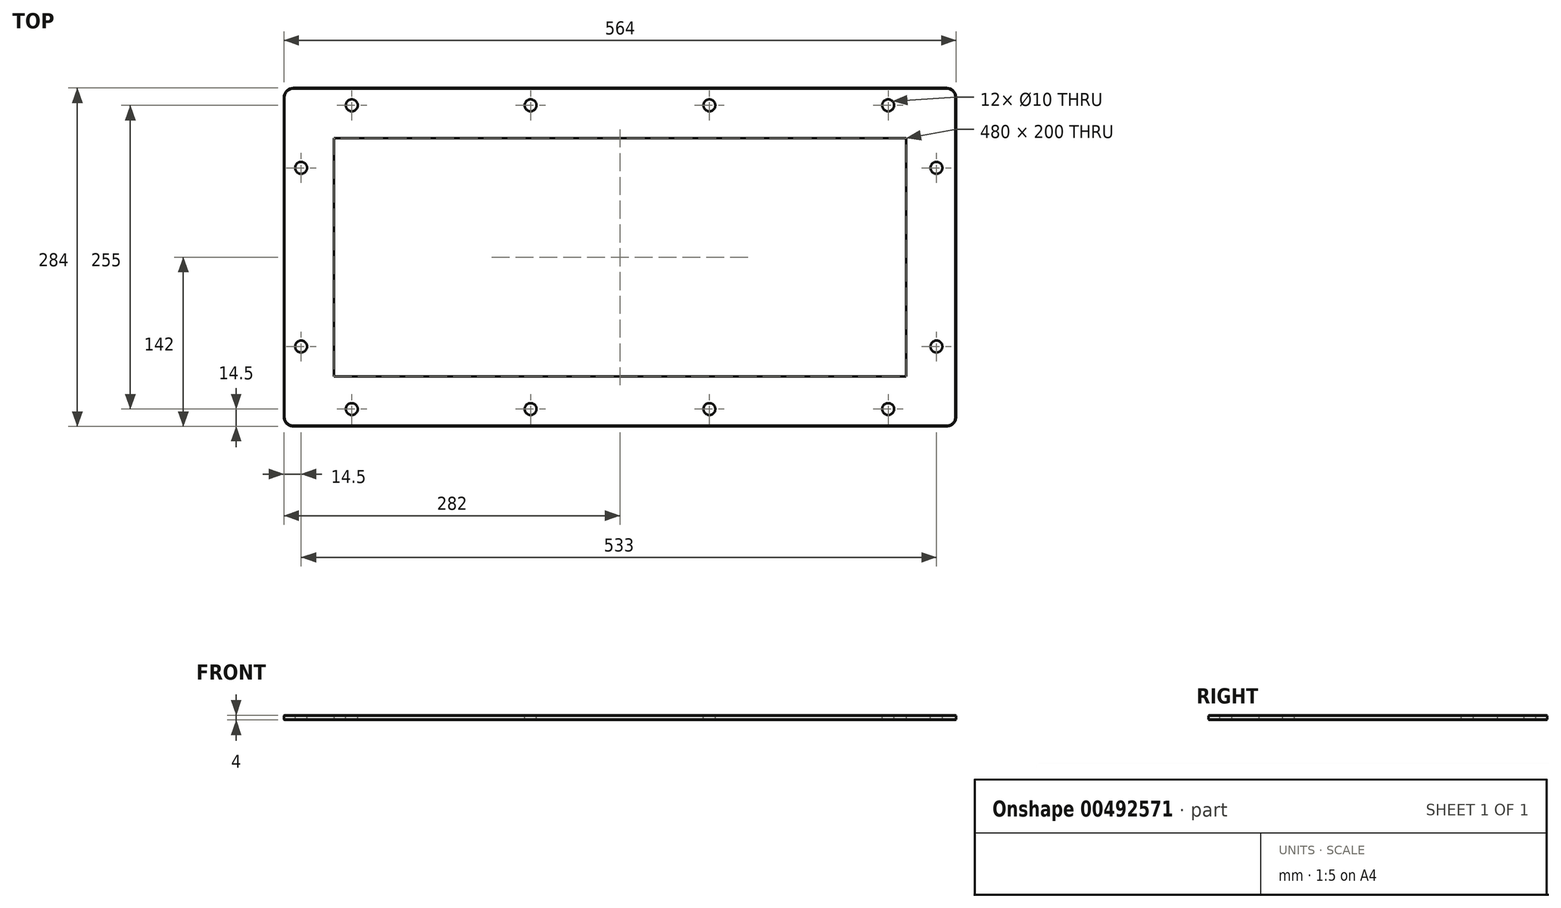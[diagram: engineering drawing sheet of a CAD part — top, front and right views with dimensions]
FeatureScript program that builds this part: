
annotation { "Feature Type Name" : "Feature", "Feature Type Description" : "" }
export const myFeature = defineFeature(function(context is Context, id is Id, definition is map)
    precondition{}
    {
        {
            var Q0;
            Q0=qCreatedBy(makeId("Top.planeOp"),FACE);
            var sketch = newSketch(context, id + "F0", { "sketchPlane" : qUnion([Q0])});
            skLineSegment(sketch, "E0.bottom", {"start": v(274, -142) * mm, "end": v(-274, -142) * mm});
            skLineSegment(sketch, "E0.top", {"start": v(274, 142) * mm, "end": v(-274, 142) * mm});
            skLineSegment(sketch, "E0.left", {"start": v(282, -134) * mm, "end": v(282, 134) * mm});
            skLineSegment(sketch, "E0.right", {"start": v(-282, -134) * mm, "end": v(-282, 134) * mm});
            skPoint(sketch, "E0.middle", {"position": v(0, 0) * mm});
            skPoint(sketch, "E1.visualSharp", {"position": v(-282, -142) * mm});
            skArc(sketch, "E1.filletArc", {"start": v(-282, -134) * mm, "mid": v(-279.66, -139.66) * mm, "end": v(-274, -142) * mm});
            skPoint(sketch, "E2.visualSharp", {"position": v(-282, 142) * mm});
            skArc(sketch, "E2.filletArc", {"start": v(-274, 142) * mm, "mid": v(-279.66, 139.66) * mm, "end": v(-282, 134) * mm});
            skPoint(sketch, "E3.visualSharp", {"position": v(282, 142) * mm});
            skArc(sketch, "E3.filletArc", {"start": v(282, 134) * mm, "mid": v(279.66, 139.66) * mm, "end": v(274, 142) * mm});
            skPoint(sketch, "E4.visualSharp", {"position": v(282, -142) * mm});
            skArc(sketch, "E4.filletArc", {"start": v(274, -142) * mm, "mid": v(279.66, -139.66) * mm, "end": v(282, -134) * mm});
            skLineSegment(sketch, "E5.0", {"start": v(-240, -100) * mm, "end": v(-240, 100) * mm});
            skLineSegment(sketch, "E5.1", {"start": v(240, -100) * mm, "end": v(-240, -100) * mm});
            skLineSegment(sketch, "E5.2", {"start": v(240, -100) * mm, "end": v(240, 100) * mm});
            skLineSegment(sketch, "E5.3", {"start": v(240, 100) * mm, "end": v(-240, 100) * mm});
            skSolve(sketch);
        }
        {
            var Q0;
            Q0=makeQuery(id+"F0.imprint","IMPRINT",FACE,{"disambiguationData":[TD([[makeQuery(id+"F0.imprint","IMPRINT",EDGE,{"derivedFrom":sQuery(id+"F0.wireOp",EDGE,"E0.bottom")}),-1.0]])]});
            extrude(context, id + "F1", {"entities" : qUnion([Q0]), "depth" : 4 * mm});
        }
        {
            var Q0;
            Q0=makeQuery(id+"F1.opExtrude","CAP_FACE",FACE,{"disambiguationData":[OSD([sQuery(id+"F0.wireOp",EDGE,"E0.bottom"),sQuery(id+"F0.wireOp",EDGE,"E0.top"),sQuery(id+"F0.wireOp",EDGE,"E0.left"),sQuery(id+"F0.wireOp",EDGE,"E0.right"),sQuery(id+"F0.wireOp",EDGE,"E1.filletArc"),sQuery(id+"F0.wireOp",EDGE,"E2.filletArc"),sQuery(id+"F0.wireOp",EDGE,"E3.filletArc"),sQuery(id+"F0.wireOp",EDGE,"E4.filletArc"),sQuery(id+"F0.wireOp",EDGE,"E5.0"),sQuery(id+"F0.wireOp",EDGE,"E5.1"),sQuery(id+"F0.wireOp",EDGE,"E5.2"),sQuery(id+"F0.wireOp",EDGE,"E5.3")])],"isStart":false});
            var sketch = newSketch(context, id + "F2", { "sketchPlane" : qUnion([Q0])});
            skLineSegment(sketch, "E6", {"start": v(-267.5, 127.5) * mm, "end": v(267.5, 127.5) * mm, "construction": true});
            skLineSegment(sketch, "E7", {"start": v(267.5, 127.5) * mm, "end": v(267.5, -127.5) * mm, "construction": true});
            skLineSegment(sketch, "E8", {"start": v(267.5, -127.5) * mm, "end": v(-267.5, -127.5) * mm, "construction": true});
            skLineSegment(sketch, "E9", {"start": v(-267.5, -127.5) * mm, "end": v(-267.5, 127.5) * mm, "construction": true});
            skLineSegment(sketch, "E10", {"start": v(-267.5, 0) * mm, "end": v(267.5, 0) * mm, "construction": true});
            skPoint(sketch, "E11", {"position": v(0, 0) * mm});
            skCircle(sketch, "E12", {"center": v(-225, 127.5) * mm, "radius": 5 * mm});
            skCircle(sketch, "E13.0.1.0", {"center": v(-225, -127.5) * mm, "radius": 5 * mm});
            skCircle(sketch, "E13.1.0.0", {"center": v(-75, 127.5) * mm, "radius": 5 * mm});
            skCircle(sketch, "E13.1.1.0", {"center": v(-75, -127.5) * mm, "radius": 5 * mm});
            skCircle(sketch, "E13.2.0.0", {"center": v(75, 127.5) * mm, "radius": 5 * mm});
            skCircle(sketch, "E13.2.1.0", {"center": v(75, -127.5) * mm, "radius": 5 * mm});
            skCircle(sketch, "E13.3.0.0", {"center": v(225, 127.5) * mm, "radius": 5 * mm});
            skCircle(sketch, "E13.3.1.0", {"center": v(225, -127.5) * mm, "radius": 5 * mm});
            skLineSegment(sketch, "E13.direction1", {"start": v(-225, 127.5) * mm, "end": v(-75, 127.5) * mm, "construction": true});
            skLineSegment(sketch, "E13.direction2", {"start": v(-225, 127.5) * mm, "end": v(-225, -127.5) * mm, "construction": true});
            skCircle(sketch, "E14", {"center": v(-267.5, 75) * mm, "radius": 5 * mm});
            skCircle(sketch, "E15.0.1.0", {"center": v(-267.5, -75) * mm, "radius": 5 * mm});
            skCircle(sketch, "E15.1.0.0", {"center": v(265.5, 75) * mm, "radius": 5 * mm});
            skCircle(sketch, "E15.1.1.0", {"center": v(265.5, -75) * mm, "radius": 5 * mm});
            skCircle(sketch, "E15.2.0.0", {"center": v(798.5, 75) * mm, "radius": 5 * mm});
            skCircle(sketch, "E15.2.1.0", {"center": v(798.5, -75) * mm, "radius": 5 * mm});
            skLineSegment(sketch, "E15.direction1", {"start": v(-267.5, 75) * mm, "end": v(265.5, 75) * mm, "construction": true});
            skLineSegment(sketch, "E15.direction2", {"start": v(-267.5, 75) * mm, "end": v(-267.5, -75) * mm, "construction": true});
            skLineSegment(sketch, "E16", {"start": v(0, 0) * mm, "end": v(0, 127.5) * mm, "construction": true});
            skSolve(sketch);
        }
        {
            var Q0;
            Q0=sQuery(id+"F2.wireOp",VERTEX,"E13.direction2.start");
            var Q1;
            Q1=sQuery(id+"F2.wireOp",VERTEX,"E13.direction1.end");
            var Q2;
            Q2=sQuery(id+"F2.wireOp",VERTEX,"E13.2.0.0.center");
            var Q3;
            Q3=sQuery(id+"F2.wireOp",VERTEX,"E13.3.0.0.center");
            var Q4;
            Q4=sQuery(id+"F2.wireOp",VERTEX,"E15.1.0.0.center");
            var Q5;
            Q5=sQuery(id+"F2.wireOp",VERTEX,"E15.1.1.0.center");
            var Q6;
            Q6=sQuery(id+"F2.wireOp",VERTEX,"E13.3.1.0.center");
            var Q7;
            Q7=sQuery(id+"F2.wireOp",VERTEX,"E13.2.1.0.center");
            var Q8;
            Q8=sQuery(id+"F2.wireOp",VERTEX,"E13.1.1.0.center");
            var Q9;
            Q9=sQuery(id+"F2.wireOp",VERTEX,"E13.0.1.0.center");
            var Q10;
            Q10=sQuery(id+"F2.wireOp",VERTEX,"E14.center");
            var Q11;
            Q11=sQuery(id+"F2.wireOp",VERTEX,"E15.0.1.0.center");
            var Q12;
            Q12=makeQuery(id+"F1.opExtrude","SWEPT_BODY",BODY,{"disambiguationData":[OSD([sQuery(id+"F0.wireOp",EDGE,"E0.bottom"),sQuery(id+"F0.wireOp",EDGE,"E0.top"),sQuery(id+"F0.wireOp",EDGE,"E0.left"),sQuery(id+"F0.wireOp",EDGE,"E0.right"),sQuery(id+"F0.wireOp",EDGE,"E1.filletArc"),sQuery(id+"F0.wireOp",EDGE,"E2.filletArc"),sQuery(id+"F0.wireOp",EDGE,"E3.filletArc"),sQuery(id+"F0.wireOp",EDGE,"E4.filletArc"),sQuery(id+"F0.wireOp",EDGE,"E5.0"),sQuery(id+"F0.wireOp",EDGE,"E5.1"),sQuery(id+"F0.wireOp",EDGE,"E5.2"),sQuery(id+"F0.wireOp",EDGE,"E5.3")])]});
            hole(context, id + "F3", {"style" : HoleStyle.SIMPLE, "endStyle" : HoleEndStyle.THROUGH, "holeDiameter" : 10 * mm, "isTappedThrough" : true, "tappedDepth" : 12 * mm, "tapClearance" : 3, "locations" : qUnion([Q0, Q1, Q2, Q3, Q4, Q5, Q6, Q7, Q8, Q9, Q10, Q11]), "scope" : qUnion([Q12])});
        }
        {
            var Q0;
            Q0=makeQuery(id+"F1.opExtrude","CAP_EDGE",EDGE,{"disambiguationData":[OSD([sQuery(id+"F0.wireOp",EDGE,"E0.bottom")])],"isStart":false});
            var Q1;
            Q1=makeQuery(id+"F1.opExtrude","SWEPT_FACE",FACE,{"disambiguationData":[OSD([sQuery(id+"F0.wireOp",EDGE,"E0.bottom")])]});
            chamfer(context, id + "F4", {"entities" : qUnion([Q0, Q1]), "width" : .5 * mm, "tangentPropagation" : true});
        }
    });
